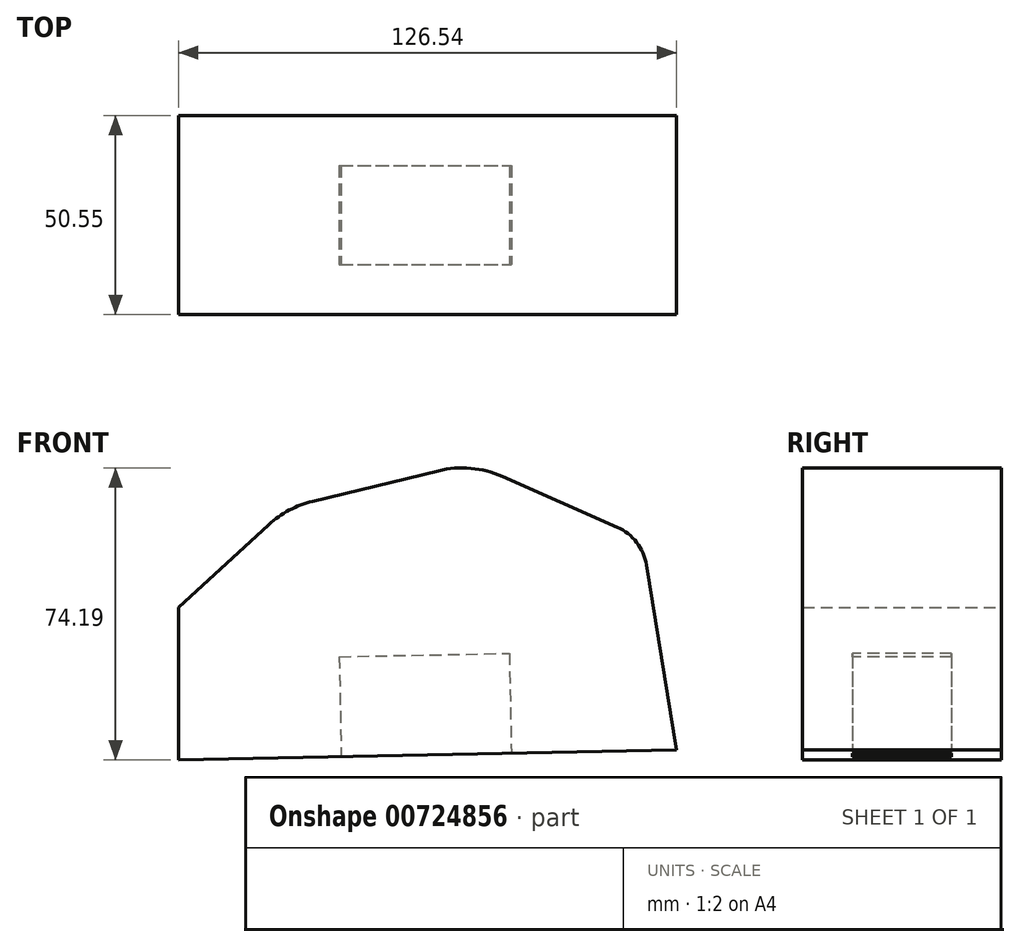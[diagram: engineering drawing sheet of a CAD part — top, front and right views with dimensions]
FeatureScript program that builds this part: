
annotation { "Feature Type Name" : "Feature", "Feature Type Description" : "" }
export const myFeature = defineFeature(function(context is Context, id is Id, definition is map)
    precondition{}
    {
        {
            var Q0;
            Q0=qCreatedBy(makeId("Front.planeOp"),FACE);
            var sketch = newSketch(context, id + "F0", { "sketchPlane" : qUnion([Q0])});
            skLineSegment(sketch, "E0", {"start": v(-59.23, -22.4) * mm, "end": v(-59.23, 16.4) * mm});
            skLineSegment(sketch, "E1", {"start": v(-59.23, 16.4) * mm, "end": v(-31.52, 41.8) * mm});
            skLineSegment(sketch, "E2", {"start": v(-31.52, 41.8) * mm, "end": v(15.12, 53.1) * mm});
            skLineSegment(sketch, "E3", {"start": v(15.12, 53.1) * mm, "end": v(58.54, 33.94) * mm});
            skLineSegment(sketch, "E4", {"start": v(58.54, 33.94) * mm, "end": v(67.31, -19.86) * mm});
            skLineSegment(sketch, "E5", {"start": v(-59.23, -22.4) * mm, "end": v(67.31, -19.86) * mm});
            skSolve(sketch);
        }
        {
            var Q0;
            Q0=makeQuery(id+"F0.imprint","IMPRINT",FACE,{"disambiguationData":[TD([[makeQuery(id+"F0.imprint","IMPRINT",EDGE,{"derivedFrom":sQuery(id+"F0.wireOp",EDGE,"E0")}),-1.0]])]});
            extrude(context, id + "F1", {"entities" : qUnion([Q0]), "depth" : 25.15 * mm, "offsetDistance" : 25.4 * mm, "hasSecondDirection" : true, "secondDirectionOppositeDirection" : true, "secondDirectionDepth" : 25.4 * mm});
        }
        {
            var Q0;
            Q0=makeQuery(id+"F1.opExtrude","SWEPT_EDGE",EDGE,{"disambiguationData":[OSD([sQuery(id+"F0.wireOp",EDGE,"E3"),sQuery(id+"F0.wireOp",EDGE,"E4")])]});
            fillet(context, id + "F2", {"entities" : qUnion([Q0]), "radius" : 12.7 * mm, "tangentPropagation" : true, "allowEdgeOverflow" : false});
        }
        {
            var Q0;
            Q0=makeQuery(id+"F1.opExtrude","SWEPT_EDGE",EDGE,{"disambiguationData":[OSD([sQuery(id+"F0.wireOp",EDGE,"E1"),sQuery(id+"F0.wireOp",EDGE,"E2")])]});
            var Q1;
            Q1=makeQuery(id+"F1.opExtrude","SWEPT_EDGE",EDGE,{"disambiguationData":[OSD([sQuery(id+"F0.wireOp",EDGE,"E2"),sQuery(id+"F0.wireOp",EDGE,"E3")])]});
            fillet(context, id + "F3", {"entities" : qUnion([Q0, Q1]), "radius" : 25.4 * mm, "tangentPropagation" : true, "allowEdgeOverflow" : false});
        }
        {
            var Q0;
            Q0=makeQuery(id+"F1.opExtrude","SWEPT_FACE",FACE,{"disambiguationData":[OSD([sQuery(id+"F0.wireOp",EDGE,"E5")])]});
            var sketch = newSketch(context, id + "F4", { "sketchPlane" : qUnion([Q0])});
            skLineSegment(sketch, "E6.bottom", {"start": v(-18.34, -12.7) * mm, "end": v(24.88, -12.7) * mm});
            skLineSegment(sketch, "E6.top", {"start": v(-18.34, 12.45) * mm, "end": v(24.88, 12.45) * mm});
            skLineSegment(sketch, "E6.left", {"start": v(-18.34, -12.7) * mm, "end": v(-18.34, 12.45) * mm});
            skLineSegment(sketch, "E6.right", {"start": v(24.88, -12.7) * mm, "end": v(24.88, 12.45) * mm});
            skSolve(sketch);
        }
        {
            var Q0;
            Q0 = qSketchRegion(id + "F4", true);
            extrude(context, id + "F5", {"entities" : qUnion([Q0]), "operationType" : NewBodyOperationType.REMOVE, "oppositeDirection" : true, "depth" : 25.4 * mm, "offsetDistance" : 25.4 * mm});
        }
    });
